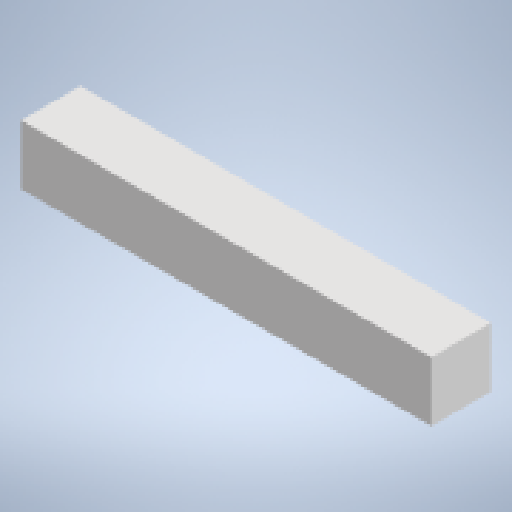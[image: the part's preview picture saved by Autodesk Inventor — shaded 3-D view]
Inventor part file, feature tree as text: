
AUTODESK INVENTOR PART (.ipt)
format: ipt  version: 2024 (Build 280153000, 153)  size: 121,856 bytes
history: native  units: mm
features: extrude x1, sketch x1
ambient origin geometry x8: Origin, YZ Plane, XZ Plane, XY Plane, X Axis, Y Axis, Z Axis, Center Point
bodies: Body1 (feature_tree)
feature tree (2):
  extrude  "Extrusion2"  Depth=45.0mm
  sketch  "Sketch2"  dims[d4=45.0mm d5=45.0mm d6=410.0mm d7=0.0mm]
